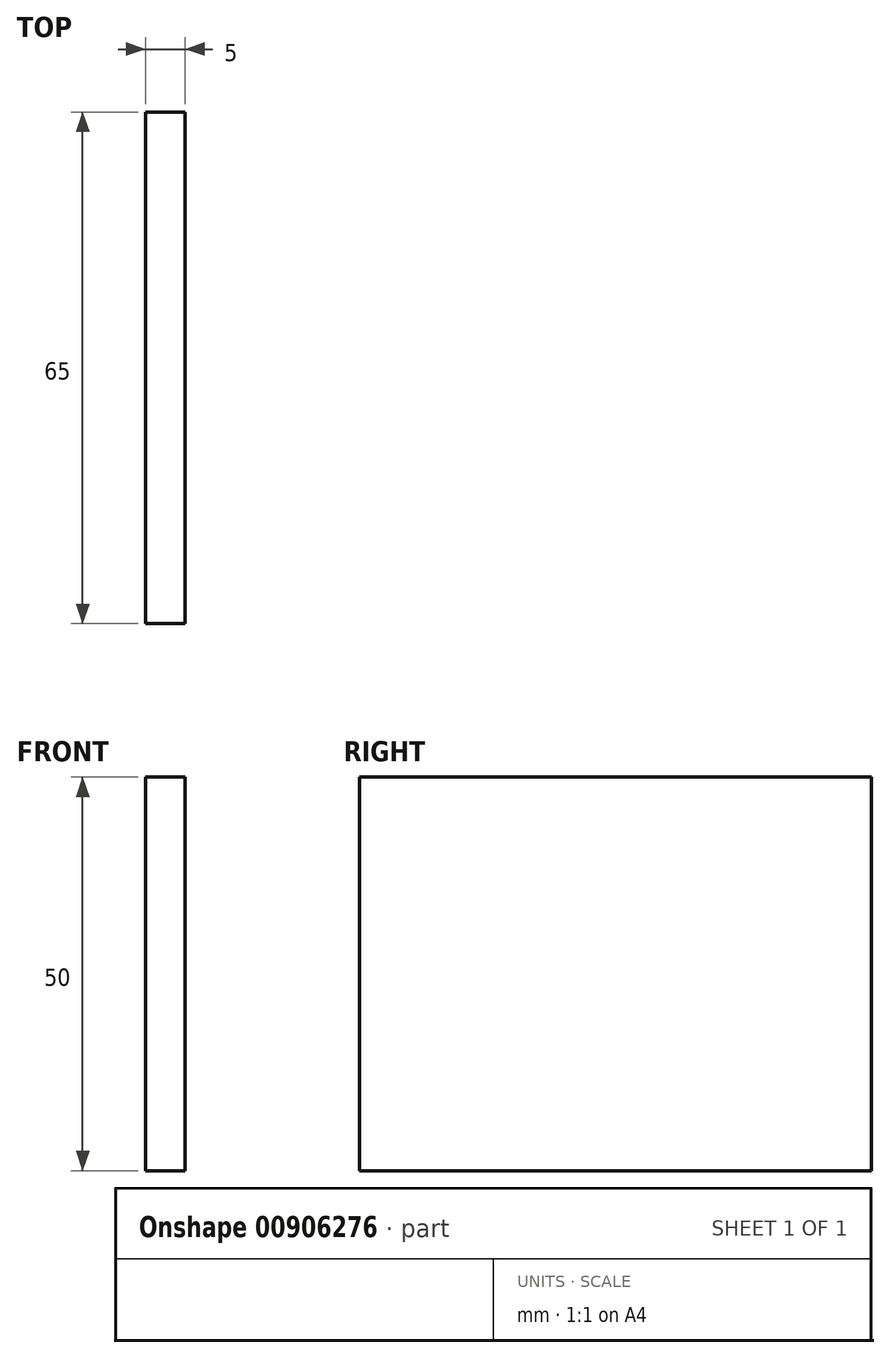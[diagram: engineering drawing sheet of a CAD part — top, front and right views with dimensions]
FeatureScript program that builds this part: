
annotation { "Feature Type Name" : "Feature", "Feature Type Description" : "" }
export const myFeature = defineFeature(function(context is Context, id is Id, definition is map)
    precondition{}
    {
        {
            var Q0;
            Q0=qCreatedBy(makeId("Top.planeOp"),FACE);
            var sketch = newSketch(context, id + "F0", { "sketchPlane" : qUnion([Q0])});
            skLineSegment(sketch, "E0", {"start": v(-17.37, 28.42) * mm, "end": v(-12.37, 28.42) * mm});
            skLineSegment(sketch, "E1", {"start": v(-12.37, 28.42) * mm, "end": v(-12.37, -36.58) * mm});
            skLineSegment(sketch, "E2", {"start": v(-12.37, -36.58) * mm, "end": v(-17.37, -36.58) * mm});
            skLineSegment(sketch, "E3", {"start": v(-17.37, -36.58) * mm, "end": v(-17.37, 28.42) * mm});
            skSolve(sketch);
        }
        {
            var Q0;
            Q0=makeQuery(id+"F0.imprint","IMPRINT",FACE,{"disambiguationData":[TD([[makeQuery(id+"F0.imprint","IMPRINT",EDGE,{"derivedFrom":sQuery(id+"F0.wireOp",EDGE,"E0")}),-1.0]])]});
            extrude(context, id + "F1", {"entities" : qUnion([Q0]), "depth" : 50 * mm, "offsetDistance" : 25 * mm});
        }
    });
